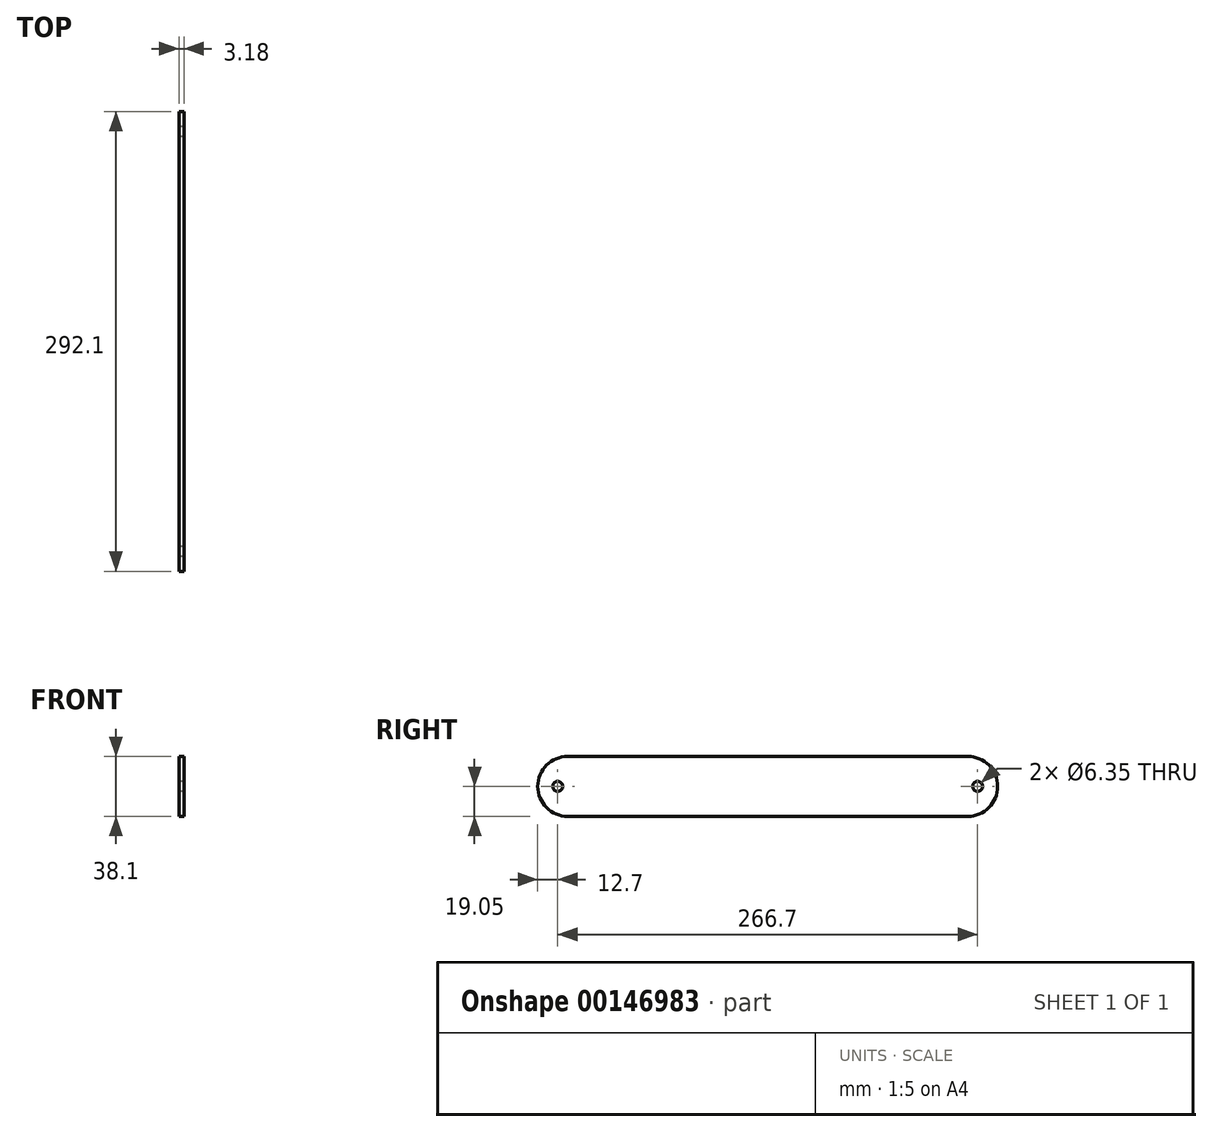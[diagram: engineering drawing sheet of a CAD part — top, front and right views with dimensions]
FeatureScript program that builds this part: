
annotation { "Feature Type Name" : "Feature", "Feature Type Description" : "" }
export const myFeature = defineFeature(function(context is Context, id is Id, definition is map)
    precondition{}
    {
        {
            var Q0;
            Q0=qCreatedBy(makeId("Right.planeOp"),FACE);
            var sketch = newSketch(context, id + "F0", { "sketchPlane" : qUnion([Q0])});
            skLineSegment(sketch, "E0.bottom", {"start": v(127, 19.05) * mm, "end": v(-127, 19.05) * mm});
            skLineSegment(sketch, "E0.top", {"start": v(127, -19.05) * mm, "end": v(-127, -19.05) * mm});
            skLineSegment(sketch, "E0.left", {"start": v(127, 19.05) * mm, "end": v(127, -19.05) * mm});
            skLineSegment(sketch, "E0.right", {"start": v(-127, 19.05) * mm, "end": v(-127, -19.05) * mm});
            skPoint(sketch, "E0.middle", {"position": v(0, 0) * mm});
            skArc(sketch, "E1", {"start": v(-127, 19.05) * mm, "mid": v(-146.05, 0) * mm, "end": v(-127, -19.05) * mm});
            skArc(sketch, "E2", {"start": v(127, -19.05) * mm, "mid": v(146.05, 0) * mm, "end": v(127, 19.05) * mm});
            skCircle(sketch, "E3", {"center": v(-133.35, 0) * mm, "radius": 3.18 * mm});
            skCircle(sketch, "E4", {"center": v(133.35, 0) * mm, "radius": 3.18 * mm});
            skSolve(sketch);
        }
        {
            var Q0;
            Q0 = qSketchRegion(id + "F0", true);
            extrude(context, id + "F1", {"entities" : qUnion([Q0]), "depth" : 3.17 * mm});
        }
    });
